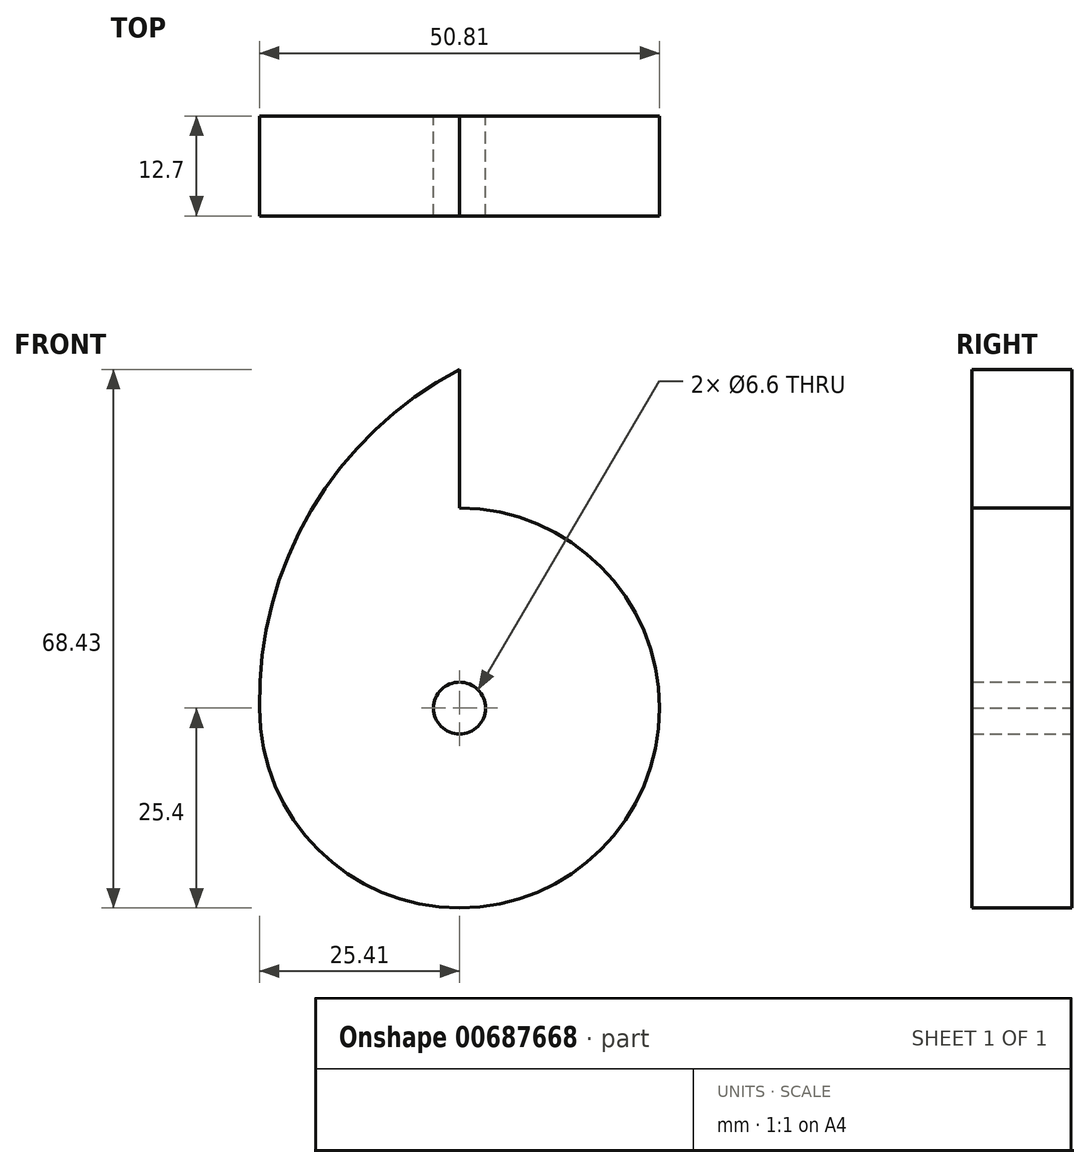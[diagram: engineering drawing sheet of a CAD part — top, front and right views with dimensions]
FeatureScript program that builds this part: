
annotation { "Feature Type Name" : "Feature", "Feature Type Description" : "" }
export const myFeature = defineFeature(function(context is Context, id is Id, definition is map)
    precondition{}
    {
        {
            var Q0;
            Q0=qCreatedBy(makeId("Front.planeOp"),FACE);
            var sketch = newSketch(context, id + "F0", { "sketchPlane" : qUnion([Q0])});
            skCircle(sketch, "E0", {"center": v(0, 0) * mm, "radius": 25.4 * mm});
            skArc(sketch, "E1", {"start": v(0, 43.03) * mm, "mid": v(-18.83, 25.13) * mm, "end": v(-25.4, 0) * mm});
            skLineSegment(sketch, "E2", {"start": v(0, 43.03) * mm, "end": v(0, 25.4) * mm});
            skCircle(sketch, "E3", {"center": v(0, 0) * mm, "radius": 3.3 * mm});
            skSolve(sketch);
        }
        {
            var Q0;
            Q0 = qSketchRegion(id + "F0", true);
            extrude(context, id + "F1", {"entities" : qUnion([Q0]), "depth" : 12.7 * mm, "offsetDistance" : 25.4 * mm});
        }
    });
